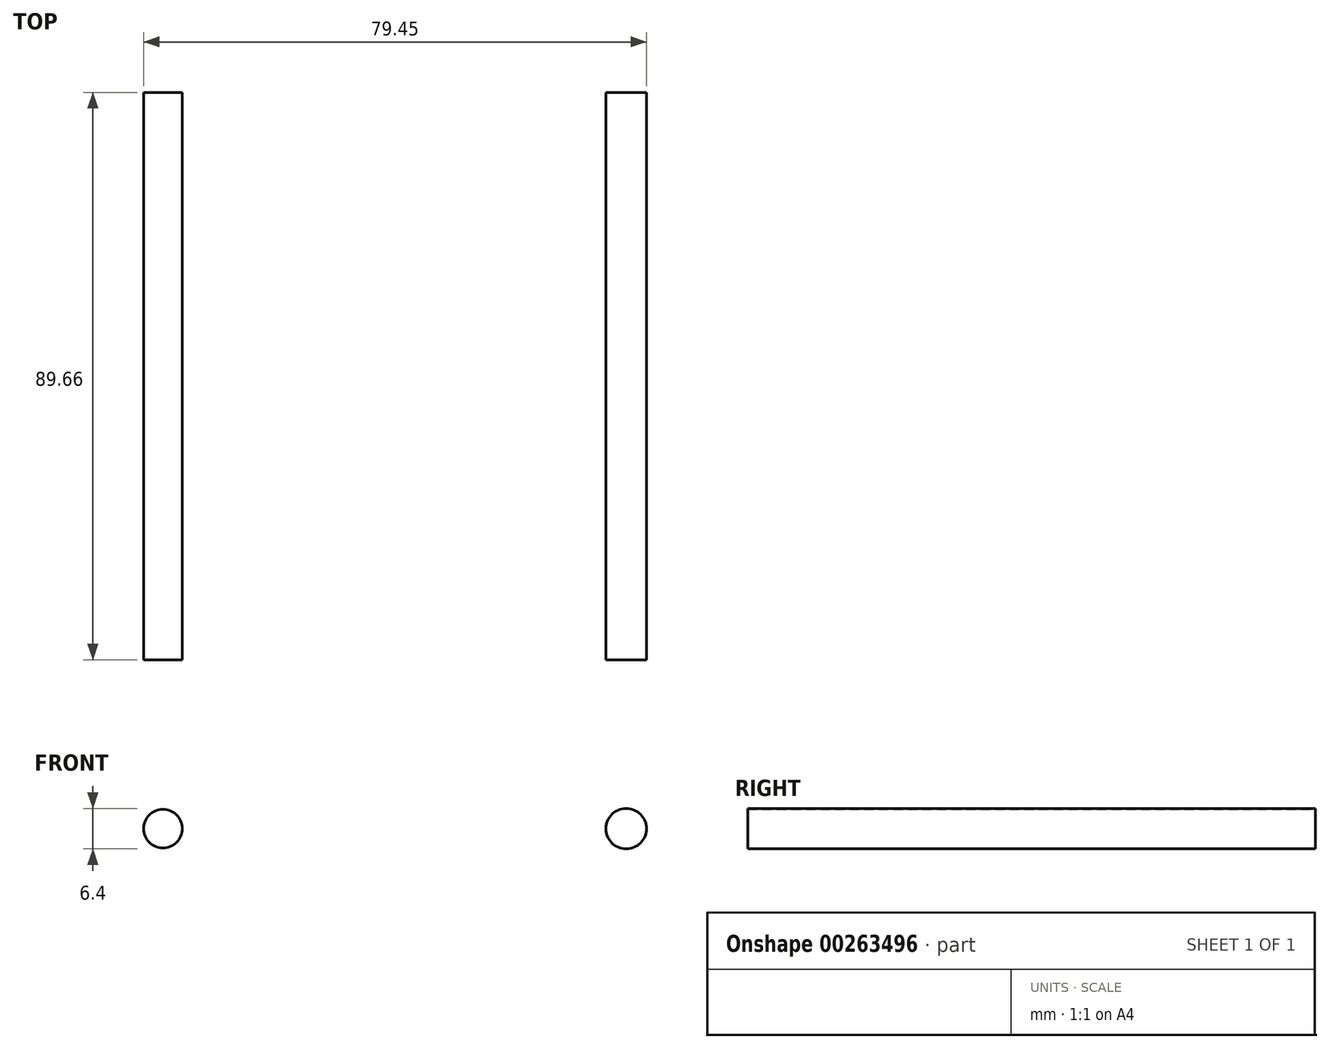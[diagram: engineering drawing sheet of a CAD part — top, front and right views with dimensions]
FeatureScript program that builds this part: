
annotation { "Feature Type Name" : "Feature", "Feature Type Description" : "" }
export const myFeature = defineFeature(function(context is Context, id is Id, definition is map)
    precondition{}
    {
        {
            var Q0;
            Q0=qCreatedBy(makeId("Front.planeOp"),FACE);
            var sketch = newSketch(context, id + "F0", { "sketchPlane" : qUnion([Q0])});
            skCircle(sketch, "E0", {"center": v(-38.83, -38.12) * mm, "radius": 3.06 * mm});
            skCircle(sketch, "E1", {"center": v(34.36, -38.12) * mm, "radius": 3.2 * mm});
            skSolve(sketch);
        }
        {
            var Q0;
            Q0 = qSketchRegion(id + "F0", true);
            extrude(context, id + "F1", {"entities" : qUnion([Q0]), "depth" : 89.66 * mm});
        }
    });
